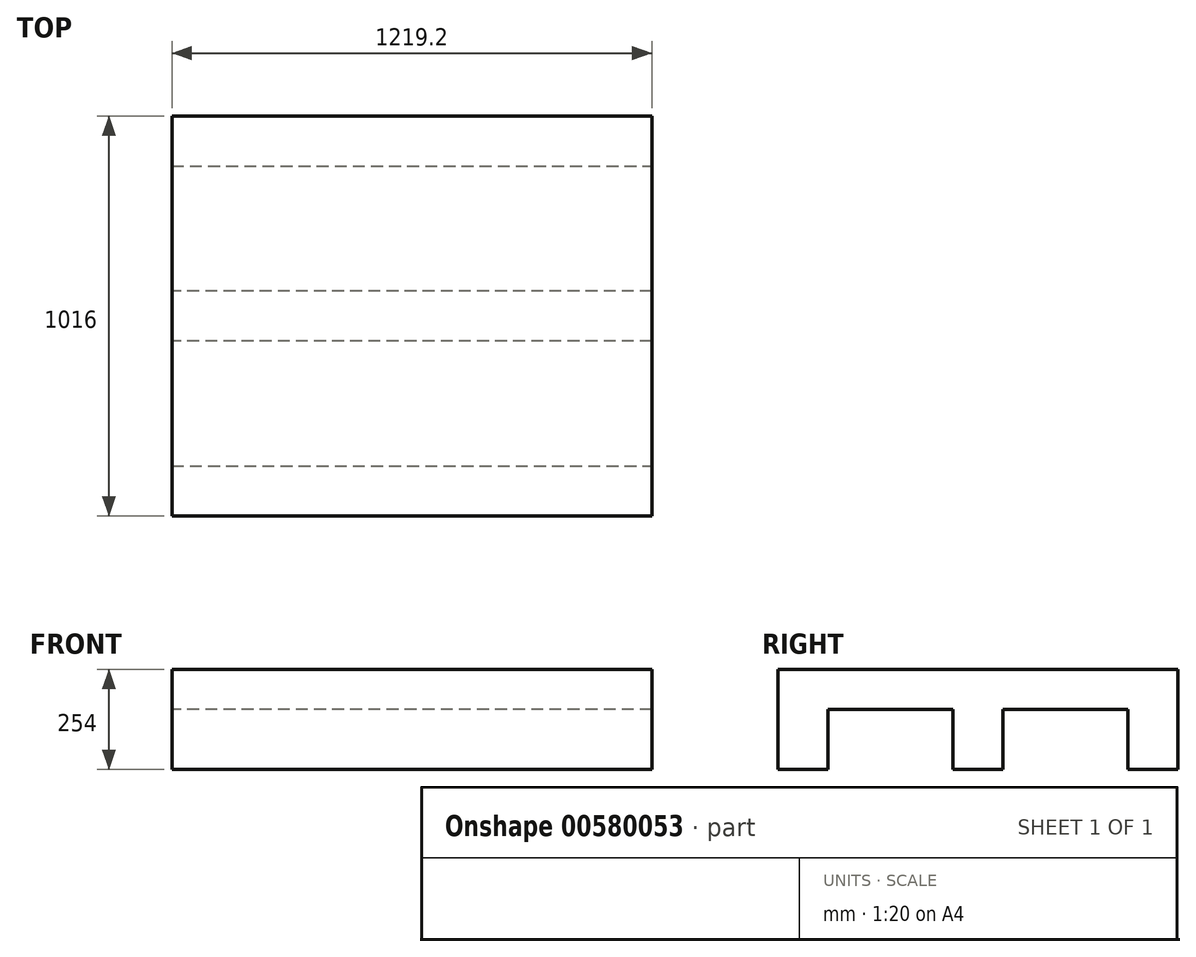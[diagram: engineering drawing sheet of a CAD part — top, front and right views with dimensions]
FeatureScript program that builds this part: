
annotation { "Feature Type Name" : "Feature", "Feature Type Description" : "" }
export const myFeature = defineFeature(function(context is Context, id is Id, definition is map)
    precondition{}
    {
        {
            var Q0;
            Q0=qCreatedBy(makeId("Top.planeOp"),FACE);
            var sketch = newSketch(context, id + "F0", { "sketchPlane" : qUnion([Q0])});
            skLineSegment(sketch, "E0.bottom", {"start": v(-609.6, 508) * mm, "end": v(609.6, 508) * mm});
            skLineSegment(sketch, "E0.top", {"start": v(-609.6, -508) * mm, "end": v(609.6, -508) * mm});
            skLineSegment(sketch, "E0.left", {"start": v(-609.6, 508) * mm, "end": v(-609.6, -508) * mm});
            skLineSegment(sketch, "E0.right", {"start": v(609.6, 508) * mm, "end": v(609.6, -508) * mm});
            skPoint(sketch, "E0.middle", {"position": v(0, 0) * mm});
            skSolve(sketch);
        }
        {
            var Q0;
            Q0 = qSketchRegion(id + "F0", true);
            extrude(context, id + "F1", {"entities" : qUnion([Q0]), "depth" : 101.6 * mm, "offsetDistance" : 25.4 * mm});
        }
        {
            var Q0;
            Q0=makeQuery(id+"F1.opExtrude","CAP_FACE",FACE,{"disambiguationData":[OSD([sQuery(id+"F0.wireOp",EDGE,"E0.bottom"),sQuery(id+"F0.wireOp",EDGE,"E0.top"),sQuery(id+"F0.wireOp",EDGE,"E0.left"),sQuery(id+"F0.wireOp",EDGE,"E0.right")])],"isStart":true});
            var sketch = newSketch(context, id + "F2", { "sketchPlane" : qUnion([Q0])});
            skLineSegment(sketch, "E1.bottom", {"start": v(-609.6, 508) * mm, "end": v(609.6, 508) * mm});
            skLineSegment(sketch, "E1.top", {"start": v(-609.6, 381) * mm, "end": v(609.6, 381) * mm});
            skLineSegment(sketch, "E1.left", {"start": v(-609.6, 508) * mm, "end": v(-609.6, 381) * mm});
            skLineSegment(sketch, "E1.right", {"start": v(609.6, 508) * mm, "end": v(609.6, 381) * mm});
            skLineSegment(sketch, "E2.bottom", {"start": v(-609.6, -508) * mm, "end": v(609.6, -508) * mm});
            skLineSegment(sketch, "E2.top", {"start": v(-609.6, -381) * mm, "end": v(609.6, -381) * mm});
            skLineSegment(sketch, "E2.left", {"start": v(-609.6, -508) * mm, "end": v(-609.6, -381) * mm});
            skLineSegment(sketch, "E2.right", {"start": v(609.6, -508) * mm, "end": v(609.6, -381) * mm});
            skLineSegment(sketch, "E3.bottom", {"start": v(609.6, -63.5) * mm, "end": v(-609.6, -63.5) * mm});
            skLineSegment(sketch, "E3.top", {"start": v(609.6, 63.5) * mm, "end": v(-609.6, 63.5) * mm});
            skLineSegment(sketch, "E3.left", {"start": v(609.6, -63.5) * mm, "end": v(609.6, 63.5) * mm});
            skLineSegment(sketch, "E3.right", {"start": v(-609.6, -63.5) * mm, "end": v(-609.6, 63.5) * mm});
            skSolve(sketch);
        }
        {
            var Q0;
            Q0 = qSketchRegion(id + "F2", true);
            extrude(context, id + "F3", {"entities" : qUnion([Q0]), "operationType" : NewBodyOperationType.ADD, "depth" : 152.4 * mm, "offsetDistance" : 25.4 * mm});
        }
    });
